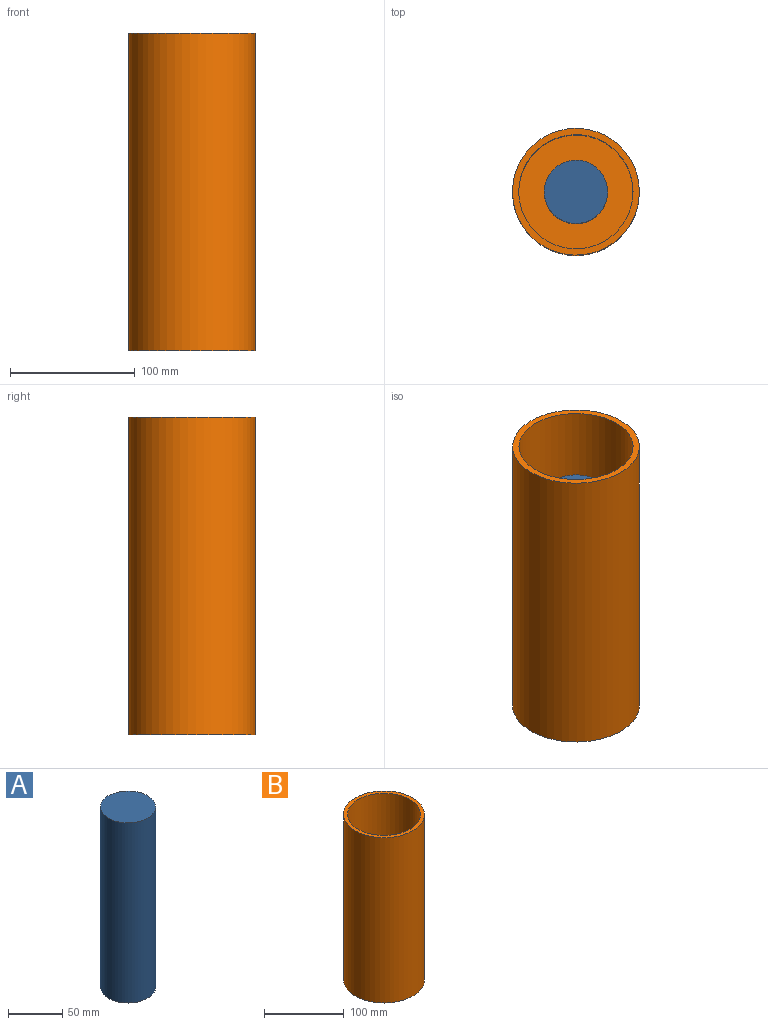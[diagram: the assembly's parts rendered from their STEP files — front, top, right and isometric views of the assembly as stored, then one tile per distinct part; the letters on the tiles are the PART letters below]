
ASSEMBLY  parts=2 mates=1
PART A: 3 faces, bbox 50.8x50.8x203.2 mm
  f0: cylinder r=25.4mm len=203.2mm, axis (0,0,-1), area 32429.3mm2, adj f1,f2
  f1: plane 50.8x50.8mm, normal (0,0,1), area 2026.8mm2, adj f0
  f2: plane 50.8x50.8mm, normal (0,0,-1), area 2026.8mm2, adj f0
PART B: 5 faces, bbox 101.6x101.6x254 mm
  f0: cylinder r=50.8mm len=254mm, axis (0,0,-1), area 81073.2mm2, adj f1,f2
  f1: plane 101.6x101.6mm, normal (0,0,1), area 1540.4mm2, adj f0,f3
  f2: plane 101.6x101.6mm, normal (0,0,-1), area 8107.3mm2, adj f0
  f3: cylinder r=45.72mm len=248.92mm, axis (0,0,-1), area 71506.6mm2, adj f1,f4
  f4: plane 91.44x91.44mm, normal (0,0,1), area 6566.9mm2, adj f3
PLACE A t=(27.01,23.58,45.89)mm
PLACE B t=(27.01,23.58,45.89)mm
MATE revolute A.f0 <-> B.f0  axis (0,0,-1) through (153.68,-92.55,101.77)mm
